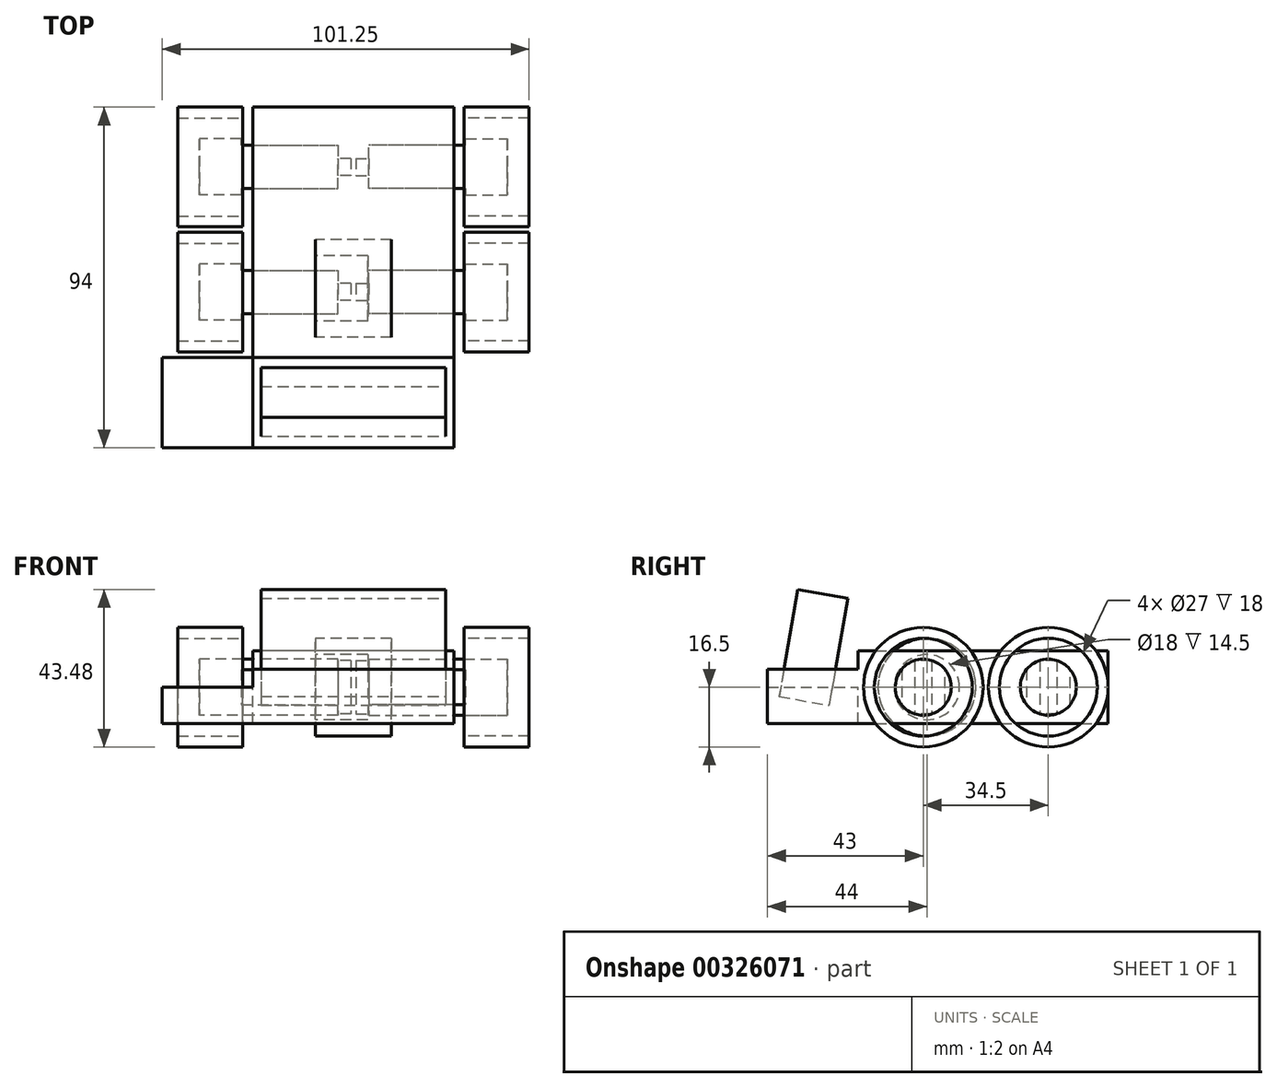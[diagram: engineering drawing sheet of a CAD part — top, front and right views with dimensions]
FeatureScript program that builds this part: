
annotation { "Feature Type Name" : "Feature", "Feature Type Description" : "" }
export const myFeature = defineFeature(function(context is Context, id is Id, definition is map)
    precondition{}
    {
        {
            assignVariable(context, id + "F0", {"name" : "GapMid", "anyValue" : 1.5 * mm});
        }
        {
            var Q0;
            Q0=qCreatedBy(makeId("Top.planeOp"),FACE);
            var sketch = newSketch(context, id + "F1", { "sketchPlane" : qUnion([Q0])});
            skLineSegment(sketch, "E0.bottom", {"start": v(-50, 50) * mm, "end": v(50, 50) * mm, "construction": true});
            skLineSegment(sketch, "E0.top", {"start": v(-50, -50) * mm, "end": v(50, -50) * mm, "construction": true});
            skLineSegment(sketch, "E0.left", {"start": v(-50, 50) * mm, "end": v(-50, -50) * mm, "construction": true});
            skLineSegment(sketch, "E0.right", {"start": v(50, 50) * mm, "end": v(50, -50) * mm, "construction": true});
            skLineSegment(sketch, "E1", {"start": v(0, 0) * mm, "end": v(39.5, 33.5) * mm, "construction": true});
            skSolve(sketch);
        }
        {
            var Q0;
            Q0=qCreatedBy(makeId("Right.planeOp"),FACE);
            var sketch = newSketch(context, id + "F2", { "sketchPlane" : qUnion([Q0])});
            skCircle(sketch, "E2", {"center": v(0, 0) * mm, "radius": 13.5 * mm});
            skCircle(sketch, "E3", {"center": v(0, 0) * mm, "radius": 16.5 * mm});
            skSolve(sketch);
        }
        {
            var Q0;
            Q0=makeQuery(id+"F2.imprint","IMPRINT",FACE,{"disambiguationData":[TD([[makeQuery(id+"F2.imprint","IMPRINT",EDGE,{"derivedFrom":sQuery(id+"F2.wireOp",EDGE,"E2")}),-1.0]])]});
            extrude(context, id + "F3", {"entities" : qUnion([Q0]), "endBound" : BoundingType.SYMMETRIC, "depth" : 18 * mm});
        }
        {
            var Q0;
            Q0=makeQuery(id+"F2.imprint","IMPRINT",FACE,{"disambiguationData":[TD([[makeQuery(id+"F2.imprint","IMPRINT",EDGE,{"derivedFrom":sQuery(id+"F2.wireOp",EDGE,"E2")}),1.0]])]});
            extrude(context, id + "F4", {"entities" : qUnion([Q0]), "endBound" : BoundingType.SYMMETRIC, "depth" : 21 * mm});
        }
        {
            var Q0;
            Q0=makeQuery(id+"F4.opExtrude","CAP_FACE",FACE,{"disambiguationData":[OSD([sQuery(id+"F2.wireOp",EDGE,"E2")])],"isStart":true});
            var sketch = newSketch(context, id + "F5", { "sketchPlane" : qUnion([Q0])});
            skCircle(sketch, "E4", {"center": v(0, 0) * mm, "radius": 9 * mm});
            skSolve(sketch);
        }
        {
            var Q0;
            Q0=makeQuery(id+"F5.imprint","IMPRINT",FACE,{"disambiguationData":[TD([[makeQuery(id+"F5.imprint","IMPRINT",EDGE,{"derivedFrom":sQuery(id+"F5.wireOp",EDGE,"E4")}),1.0]])]});
            var Q1;
            Q1=sQuery(id+"F5.wireOp",EDGE,"E4");
            extrude(context, id + "F6", {"entities" : qUnion([Q0]), "operationType" : NewBodyOperationType.REMOVE, "surfaceEntities" : qUnion([Q1]), "oppositeDirection" : true, "depth" : 14.5 * mm});
        }
        {
            var Q0;
            Q0=makeQuery(id+"F6.boolean.opBoolean","COPY",FACE,{"derivedFrom":makeQuery(id+"F6.opExtrude","CAP_FACE",FACE,{"disambiguationData":[OSD([sQuery(id+"F5.wireOp",EDGE,"E4")])],"isStart":false})});
            cPlane(context, id + "F7", {"entities" : qUnion([Q0]), "cplaneType" : CPlaneType.OFFSET, "offset" : 1 * mm, "width" : 150 * mm, "height" : 150 * mm});
        }
        {
            var Q0;
            Q0=qCreatedBy(id+"F7.planeOp",FACE);
            var sketch = newSketch(context, id + "F8", { "sketchPlane" : qUnion([Q0])});
            skCircle(sketch, "E5", {"center": v(0, 0) * mm, "radius": 7.73 * mm});
            skSolve(sketch);
        }
        {
            var Q0;
            Q0=makeQuery(id+"F8.imprint","IMPRINT",FACE,{"disambiguationData":[TD([[makeQuery(id+"F8.imprint","IMPRINT",EDGE,{"derivedFrom":sQuery(id+"F8.wireOp",EDGE,"E5")}),1.0]])]});
            extrude(context, id + "F9", {"entities" : qUnion([Q0]), "depth" : 38.22 * mm});
        }
        {
            var Q0;
            Q0=makeQuery(id+"F9.opExtrude","CAP_FACE",FACE,{"disambiguationData":[OSD([sQuery(id+"F8.wireOp",EDGE,"E5")])],"isStart":false});
            var sketch = newSketch(context, id + "F10", { "sketchPlane" : qUnion([Q0])});
            skLineSegment(sketch, "E6", {"start": v(-6, 0) * mm, "end": v(6, 0) * mm, "construction": true});
            skLineSegment(sketch, "E7", {"start": v(-6, -4.87) * mm, "end": v(-6, 4.87) * mm});
            skLineSegment(sketch, "E8", {"start": v(6, 4.87) * mm, "end": v(6, -4.87) * mm});
            skSolve(sketch);
        }
        {
            var Q0;
            {var subQ0=sQuery(id+"F10.wireOp",EDGE,"E7");Q0=makeQuery(id+"F10.imprint","IMPRINT",FACE,{"disambiguationData":[TD([[makeQuery(id+"F10.imprint","IMPRINT",EDGE,{"derivedFrom":subQ0}),1.0]])]});}
            var Q1;
            {var subQ0=sQuery(id+"F10.wireOp",EDGE,"E8");Q1=makeQuery(id+"F10.imprint","IMPRINT",FACE,{"disambiguationData":[TD([[makeQuery(id+"F10.imprint","IMPRINT",EDGE,{"derivedFrom":subQ0}),1.0]])]});}
            extrude(context, id + "F11", {"entities" : qUnion([Q0, Q1]), "operationType" : NewBodyOperationType.REMOVE, "oppositeDirection" : true, "depth" : 26.7 * mm});
        }
        {
            var Q0;
            Q0=makeQuery(id+"F9.opExtrude","CAP_FACE",FACE,{"disambiguationData":[OSD([sQuery(id+"F8.wireOp",EDGE,"E5")])],"isStart":false});
            var sketch = newSketch(context, id + "F12", { "sketchPlane" : qUnion([Q0])});
            skLineSegment(sketch, "E9", {"start": v(-2.35, 7.36) * mm, "end": v(2.35, 7.36) * mm});
            skLineSegment(sketch, "E10", {"start": v(-2.35, -7.36) * mm, "end": v(2.35, -7.36) * mm});
            skLineSegment(sketch, "E11", {"start": v(-2.35, 7.36) * mm, "end": v(-2.35, -7.36) * mm});
            skLineSegment(sketch, "E12", {"start": v(2.35, 7.36) * mm, "end": v(2.35, -7.36) * mm});
            skSolve(sketch);
        }
        {
            var Q0;
            Q0=makeQuery(id+"F12.imprint","IMPRINT",FACE,{"disambiguationData":[TD([[makeQuery(id+"F12.imprint","IMPRINT",EDGE,{"derivedFrom":sQuery(id+"F12.wireOp",EDGE,"E9")}),-1.0]])]});
            extrude(context, id + "F13", {"entities" : qUnion([Q0]), "operationType" : NewBodyOperationType.ADD, "depth" : 3.6 * mm});
        }
        {
            var Q0;
            Q0=makeQuery(id+"F3.opExtrude","SWEPT_BODY",BODY,{"disambiguationData":[OSD([sQuery(id+"F2.wireOp",EDGE,"E2"),sQuery(id+"F2.wireOp",EDGE,"E3")])]});
            var Q1;
            Q1=makeQuery(id+"F9.opExtrude","SWEPT_BODY",BODY,{"disambiguationData":[OSD([sQuery(id+"F8.wireOp",EDGE,"E5")])]});
            var Q2;
            Q2=sQuery(id+"F1.wireOp",EDGE,"E1");
            transform(context, id + "F14", {"entities" : qUnion([Q0, Q1]), "transformType" : TransformType.TRANSLATION_ENTITY, "oppositeDirectionEntity" : false, "transformLine" : qUnion([Q2]), "makeCopy" : false});
        }
        {
            var Q0;
            Q0=makeQuery(id+"F3.opExtrude","SWEPT_BODY",BODY,{"disambiguationData":[OSD([sQuery(id+"F2.wireOp",EDGE,"E2"),sQuery(id+"F2.wireOp",EDGE,"E3")])]});
            var Q1;
            Q1=makeQuery(id+"F9.opExtrude","SWEPT_BODY",BODY,{"disambiguationData":[OSD([sQuery(id+"F8.wireOp",EDGE,"E5")])]});
            var Q2;
            Q2=qCreatedBy(makeId("Right.planeOp"),FACE);
            mirror(context, id + "F15", {"entities" : qUnion([Q0, Q1]), "mirrorPlane" : qUnion([Q2])});
        }
        {
            var Q0;
            Q0=makeQuery(id+"F15.opPattern","COPY",BODY,{"derivedFrom":makeQuery(id+"F3.opExtrude","SWEPT_BODY",BODY,{"disambiguationData":[OSD([sQuery(id+"F2.wireOp",EDGE,"E2"),sQuery(id+"F2.wireOp",EDGE,"E3")])]}),"instanceName":"1"});
            var Q1;
            Q1=makeQuery(id+"F3.opExtrude","SWEPT_BODY",BODY,{"disambiguationData":[OSD([sQuery(id+"F2.wireOp",EDGE,"E2"),sQuery(id+"F2.wireOp",EDGE,"E3")])]});
            var Q2;
            Q2=makeQuery(id+"F9.opExtrude","SWEPT_BODY",BODY,{"disambiguationData":[OSD([sQuery(id+"F8.wireOp",EDGE,"E5")])]});
            var Q3;
            Q3=makeQuery(id+"F15.opPattern","COPY",BODY,{"derivedFrom":makeQuery(id+"F9.opExtrude","SWEPT_BODY",BODY,{"disambiguationData":[OSD([sQuery(id+"F8.wireOp",EDGE,"E5")])]}),"instanceName":"1"});
            var Q4;
            Q4=makeQuery(id+"F15.opPattern","COPY",FACE,{"derivedFrom":makeQuery(id+"F11.boolean.opBoolean","COPY",FACE,{"derivedFrom":makeQuery(id+"F11.opExtrude","SWEPT_FACE",FACE,{"disambiguationData":[OSD([sQuery(id+"F10.wireOp",EDGE,"E8")])]})}),"instanceName":"1"});
            transform(context, id + "F16", {"entities" : qUnion([Q0, Q1, Q2, Q3]), "transformType" : TransformType.TRANSLATION_DISTANCE, "transformDirection" : qUnion([Q4]), "distance" : getVariable(context, 'GapMid') + 33 * mm, "makeCopy" : true});
        }
        {
            var Q0;
            Q0=makeQuery(id+"F16.opPattern","COPY",FACE,{"derivedFrom":makeQuery(id+"F15.opPattern","COPY",FACE,{"derivedFrom":makeQuery(id+"F4.opExtrude","CAP_FACE",FACE,{"disambiguationData":[OSD([sQuery(id+"F2.wireOp",EDGE,"E2")])],"isStart":false}),"instanceName":"1"}),"instanceName":"1"});
            var sketch = newSketch(context, id + "F17", { "sketchPlane" : qUnion([Q0])});
            skPoint(sketch, "E13", {"position": v(1, 0) * mm});
            skLineSegment(sketch, "E14", {"start": v(1, -5.4) * mm, "end": v(1, 5.4) * mm});
            skSolve(sketch);
        }
        {
            var Q0;
            Q0=qCreatedBy(makeId("Top.planeOp"),FACE);
            var sketch = newSketch(context, id + "F18", { "sketchPlane" : qUnion([Q0])});
            skLineSegment(sketch, "E15.bottom", {"start": v(27.75, -19) * mm, "end": v(-27.75, -19) * mm});
            skLineSegment(sketch, "E15.top", {"start": v(27.75, 50) * mm, "end": v(-27.75, 50) * mm});
            skLineSegment(sketch, "E15.left", {"start": v(27.75, -19) * mm, "end": v(27.75, 50) * mm});
            skLineSegment(sketch, "E15.right", {"start": v(-27.75, -19) * mm, "end": v(-27.75, 50) * mm});
            skSolve(sketch);
        }
        {
            var Q0;
            Q0=makeQuery(id+"F18.imprint","IMPRINT",FACE,{"disambiguationData":[TD([[makeQuery(id+"F18.imprint","IMPRINT",EDGE,{"derivedFrom":sQuery(id+"F18.wireOp",EDGE,"E15.bottom")}),-1.0]])]});
            extrude(context, id + "F19", {"entities" : qUnion([Q0]), "oppositeDirection" : true, "depth" : 10 * mm});
        }
        {
            var Q0;
            Q0=makeQuery(id+"F18.imprint","IMPRINT",FACE,{"disambiguationData":[TD([[makeQuery(id+"F18.imprint","IMPRINT",EDGE,{"derivedFrom":sQuery(id+"F18.wireOp",EDGE,"E15.bottom")}),-1.0]])]});
            var sketch = newSketch(context, id + "F20", { "sketchPlane" : qUnion([Q0])});
            skLineSegment(sketch, "E16.bottom", {"start": v(-25.5, 15) * mm, "end": v(25.5, 15) * mm});
            skLineSegment(sketch, "E16.top", {"start": v(-25.5, -15) * mm, "end": v(25.5, -15) * mm});
            skLineSegment(sketch, "E16.left", {"start": v(-25.5, 15) * mm, "end": v(-25.5, -15) * mm});
            skLineSegment(sketch, "E16.right", {"start": v(25.5, 15) * mm, "end": v(25.5, -15) * mm});
            skLineSegment(sketch, "E17", {"start": v(0, -15) * mm, "end": v(0, 15) * mm, "construction": true});
            skSolve(sketch);
        }
        {
            var Q0;
            Q0=qSketchRegion(id+"F20",true);
            extrude(context, id + "F21", {"entities" : qUnion([Q0]), "depth" : 14 * mm});
        }
        {
            var Q0;
            Q0=makeQuery(id+"F21.opExtrude","SWEPT_BODY",BODY,{"disambiguationData":[OSD([sQuery(id+"F20.wireOp",EDGE,"E16.bottom"),sQuery(id+"F20.wireOp",EDGE,"E16.top"),sQuery(id+"F20.wireOp",EDGE,"E16.left"),sQuery(id+"F20.wireOp",EDGE,"E16.right")])]});
            var Q1;
            Q1=makeQuery(id+"F21.opExtrude","CAP_EDGE",EDGE,{"disambiguationData":[OSD([sQuery(id+"F20.wireOp",EDGE,"E16.top")])],"isStart":true});
            transform(context, id + "F22", {"entities" : qUnion([Q0]), "transformType" : TransformType.ROTATION, "transformAxis" : qUnion([Q1]), "angle" : 80 * degree, "makeCopy" : false});
        }
        {
            var Q0;
            Q0=makeQuery(id+"F21.opExtrude","SWEPT_BODY",BODY,{"disambiguationData":[OSD([sQuery(id+"F20.wireOp",EDGE,"E16.bottom"),sQuery(id+"F20.wireOp",EDGE,"E16.top"),sQuery(id+"F20.wireOp",EDGE,"E16.left"),sQuery(id+"F20.wireOp",EDGE,"E16.right")])]});
            transform(context, id + "F23", {"entities" : qUnion([Q0]), "transformType" : TransformType.TRANSLATION_3D, "dx" : 0 * mm, "dy" : -12 * mm, "dz" : -5 * mm, "makeCopy" : false});
        }
        {
            var Q0;
            Q0=makeQuery(id+"F19.opExtrude","CAP_FACE",FACE,{"disambiguationData":[OSD([sQuery(id+"F18.wireOp",EDGE,"E15.bottom"),sQuery(id+"F18.wireOp",EDGE,"E15.top"),sQuery(id+"F18.wireOp",EDGE,"E15.left"),sQuery(id+"F18.wireOp",EDGE,"E15.right")])],"isStart":true});
            extrude(context, id + "F24", {"entities" : qUnion([Q0]), "depth" : 10 * mm});
        }
        {
            var Q0;
            Q0=makeQuery(id+"F19.opExtrude","SWEPT_FACE",FACE,{"disambiguationData":[OSD([sQuery(id+"F18.wireOp",EDGE,"E15.bottom")])]});
            extrude(context, id + "F25", {"entities" : qUnion([Q0]), "depth" : 25 * mm});
        }
        {
            var Q0;
            {var subQ0=sQuery(id+"F18.wireOp",EDGE,"E15.bottom");Q0=makeQuery(id+"F25.opExtrude","SWEPT_FACE",FACE,{"disambiguationData":[OSD([subQ0]),TDD([makeQuery(id+"F19.opExtrude","CAP_EDGE",EDGE,{"disambiguationData":[OSD([subQ0])],"isStart":true})])]});}
            extrude(context, id + "F26", {"entities" : qUnion([Q0]), "depth" : 5 * mm});
        }
        {
            var Q0;
            Q0=makeQuery(id+"F25.opExtrude","SWEPT_FACE",FACE,{"disambiguationData":[OSD([sQuery(id+"F18.wireOp",EDGE,"E15.bottom"),sQuery(id+"F18.wireOp",EDGE,"E15.right")])]});
            extrude(context, id + "F27", {"entities" : qUnion([Q0]), "operationType" : NewBodyOperationType.ADD, "depth" : 25 * mm});
        }
    });
